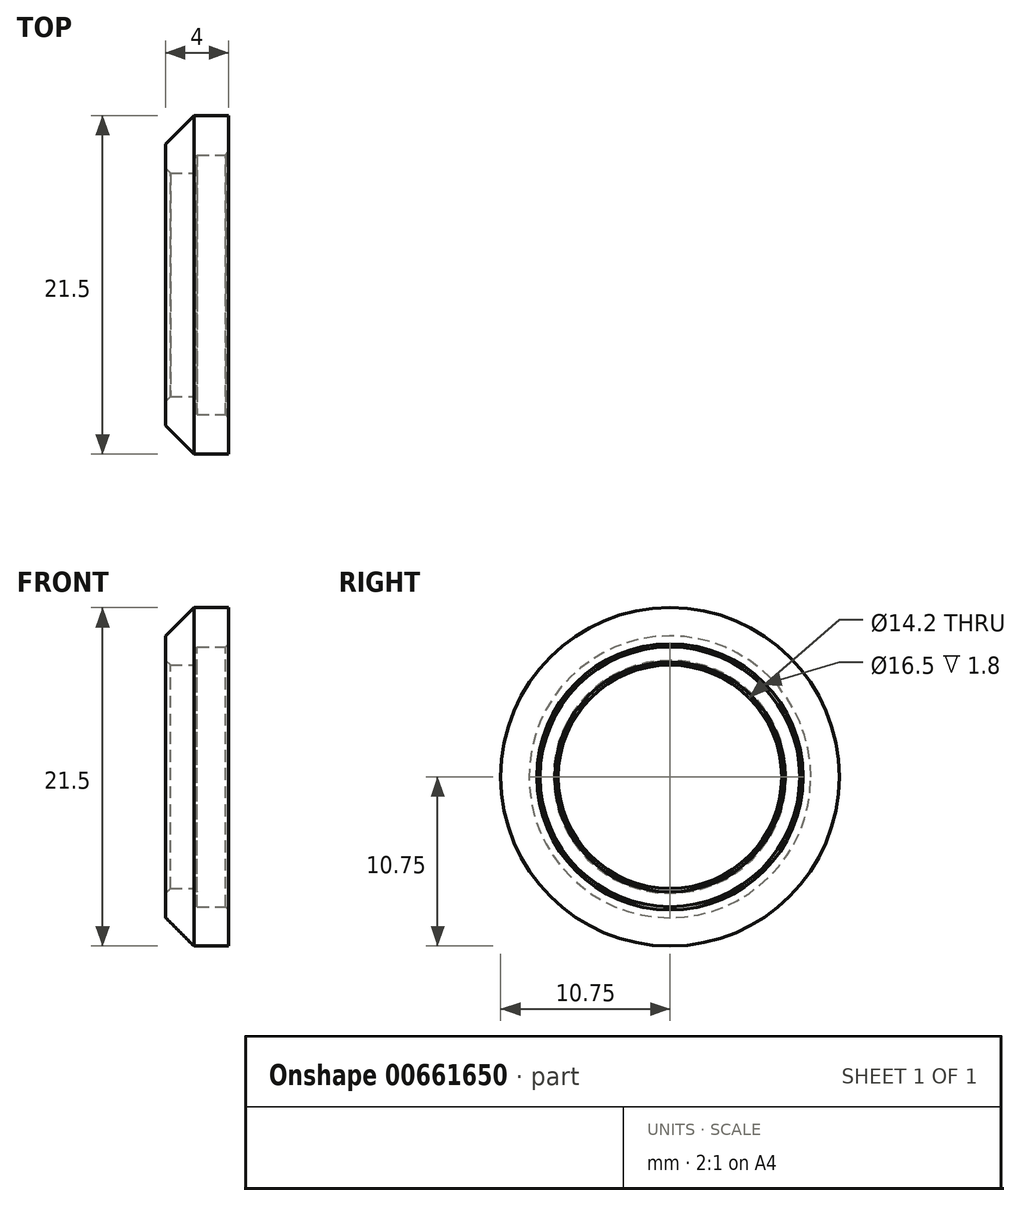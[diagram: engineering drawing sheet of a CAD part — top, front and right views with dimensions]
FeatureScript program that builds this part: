
annotation { "Feature Type Name" : "Feature", "Feature Type Description" : "" }
export const myFeature = defineFeature(function(context is Context, id is Id, definition is map)
    precondition{}
    {
        {
            var Q0;
            Q0=qCreatedBy(makeId("Top.planeOp"),FACE);
            var sketch = newSketch(context, id + "F0", { "sketchPlane" : qUnion([Q0])});
            skLineSegment(sketch, "E0", {"start": v(0, 7.1) * mm, "end": v(-2, 7.1) * mm});
            skLineSegment(sketch, "E1", {"start": v(-2, 7.1) * mm, "end": v(-2, 10.75) * mm});
            skLineSegment(sketch, "E2", {"start": v(-2, 10.75) * mm, "end": v(2, 10.75) * mm});
            skLineSegment(sketch, "E3", {"start": v(0, 0) * mm, "end": v(-2, 0) * mm, "construction": true});
            skLineSegment(sketch, "E4", {"start": v(0, 7.1) * mm, "end": v(0, 8.25) * mm});
            skLineSegment(sketch, "E5", {"start": v(0, 8.25) * mm, "end": v(2, 8.25) * mm});
            skLineSegment(sketch, "E6", {"start": v(2, 8.25) * mm, "end": v(2, 10.75) * mm});
            skSolve(sketch);
        }
        {
            var Q0;
            Q0=makeQuery(id+"F0.imprint","IMPRINT",FACE,{"disambiguationData":[TD([[makeQuery(id+"F0.imprint","IMPRINT",EDGE,{"derivedFrom":sQuery(id+"F0.wireOp",EDGE,"E0")}),-1.0]])]});
            var Q1;
            Q1=sQuery(id+"F0.wireOp",EDGE,"E3");
            revolve(context, id + "F1", {"entities" : qUnion([Q0]), "axis" : qUnion([Q1]), "revolveType" : RevolveType.FULL});
        }
        {
            var Q0;
            Q0=makeQuery(id+"F1.opRevolve","SWEPT_EDGE",EDGE,{"disambiguationData":[OSD([sQuery(id+"F0.wireOp",EDGE,"E1"),sQuery(id+"F0.wireOp",EDGE,"E2")])]});
            chamfer(context, id + "F2", {"entities" : qUnion([Q0]), "width" : 1.8 * mm, "tangentPropagation" : true});
        }
        {
            var Q0;
            Q0=makeQuery(id+"F1.opRevolve","SWEPT_EDGE",EDGE,{"disambiguationData":[OSD([sQuery(id+"F0.wireOp",EDGE,"E0"),sQuery(id+"F0.wireOp",EDGE,"E1")])]});
            chamfer(context, id + "F3", {"entities" : qUnion([Q0]), "width" : 0.3 * mm, "tangentPropagation" : true});
        }
        {
            var Q0;
            Q0=makeQuery(id+"F1.opRevolve","SWEPT_EDGE",EDGE,{"disambiguationData":[OSD([sQuery(id+"F0.wireOp",EDGE,"E5"),sQuery(id+"F0.wireOp",EDGE,"E6")])]});
            var Q1;
            Q1=makeQuery(id+"F1.opRevolve","SWEPT_EDGE",EDGE,{"disambiguationData":[OSD([sQuery(id+"F0.wireOp",EDGE,"E0"),sQuery(id+"F0.wireOp",EDGE,"E4")])]});
            chamfer(context, id + "F4", {"entities" : qUnion([Q0, Q1]), "width" : 0.2 * mm, "tangentPropagation" : true});
        }
    });
